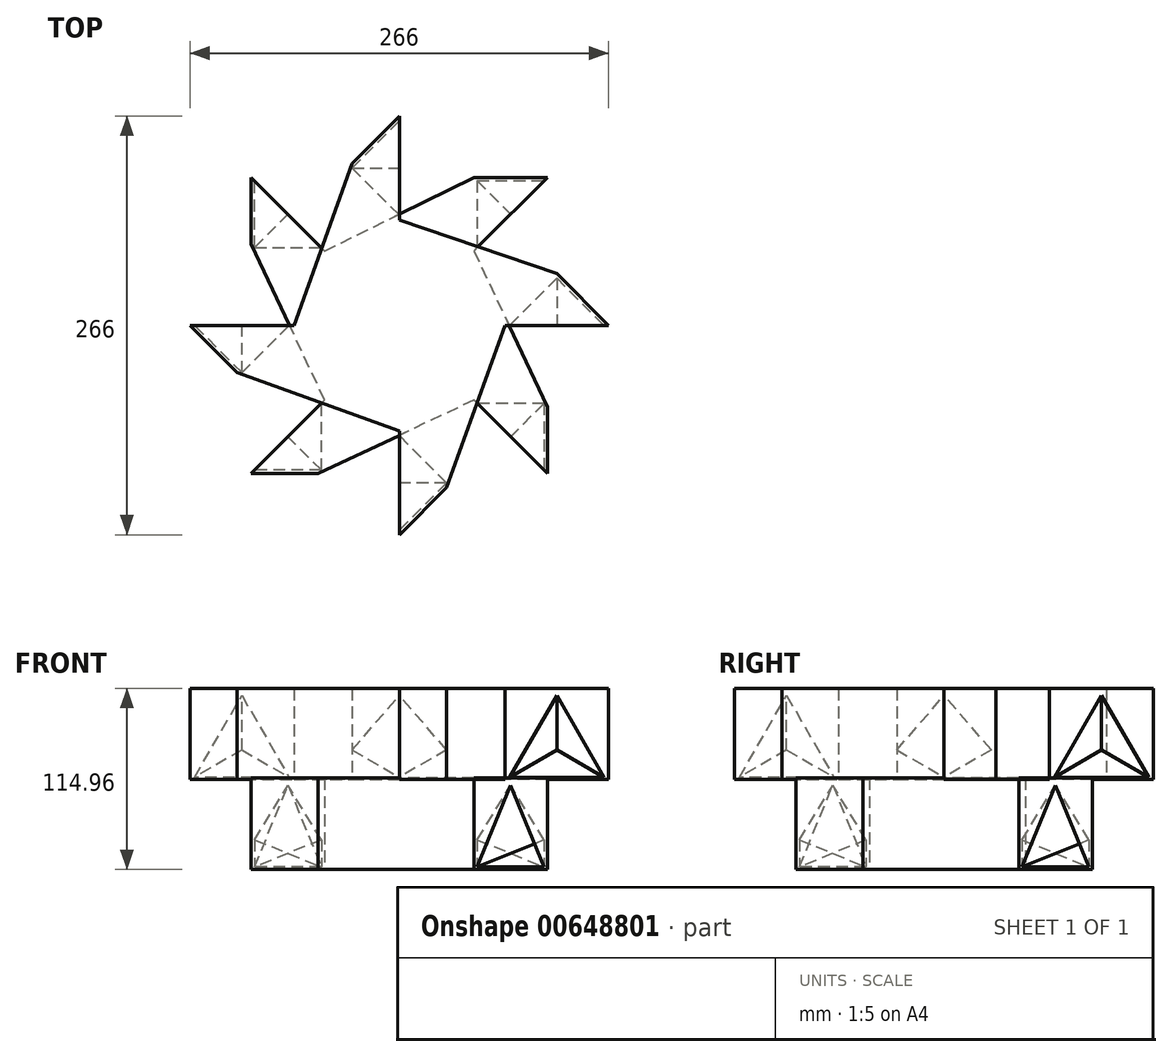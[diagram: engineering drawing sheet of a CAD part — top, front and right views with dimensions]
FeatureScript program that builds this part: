
annotation { "Feature Type Name" : "Feature", "Feature Type Description" : "" }
export const myFeature = defineFeature(function(context is Context, id is Id, definition is map)
    precondition{}
    {
        {
            var Q0;
            Q0=qCreatedBy(makeId("Front.planeOp"),FACE);
            var sketch = newSketch(context, id + "F0", { "sketchPlane" : qUnion([Q0])});
            skLineSegment(sketch, "E0", {"start": v(0, 0) * mm, "end": v(0, 38.88) * mm, "construction": true});
            skLineSegment(sketch, "E1", {"start": v(0, 0) * mm, "end": v(100, 0) * mm, "construction": true});
            skCircle(sketch, "E2.cCircle", {"center": v(100, 18.82) * mm, "radius": 34.64 * mm, "construction": true});
            skLineSegment(sketch, "E2.0", {"start": v(130, 1.5) * mm, "end": v(70, 1.5) * mm});
            skLineSegment(sketch, "E2.1", {"start": v(70, 1.5) * mm, "end": v(100, 53.46) * mm});
            skLineSegment(sketch, "E2.2", {"start": v(100, 53.46) * mm, "end": v(130, 1.5) * mm});
            skLineSegment(sketch, "E3", {"start": v(100, 0) * mm, "end": v(100, 18.82) * mm, "construction": true});
            skSolve(sketch);
        }
        {
            var Q0;
            Q0=makeQuery(id+"F0.imprint","IMPRINT",FACE,{"disambiguationData":[TD([[makeQuery(id+"F0.imprint","IMPRINT",EDGE,{"derivedFrom":sQuery(id+"F0.wireOp",EDGE,"E2.0")}),-1.0]])]});
            extrude(context, id + "F1", {"entities" : qUnion([Q0]), "oppositeDirection" : true, "depth" : 31 * mm, "offsetDistance" : 25 * mm, "hasDraft" : true, "draftAngle" : 30 * degree, "draftPullDirection" : true});
        }
        {
            var Q0;
            Q0=makeQuery(id+"F1.opExtrude","SWEPT_BODY",BODY,{"disambiguationData":[OSD([sQuery(id+"F0.wireOp",EDGE,"E2.0"),sQuery(id+"F0.wireOp",EDGE,"E2.1"),sQuery(id+"F0.wireOp",EDGE,"E2.2")])]});
            var Q1;
            Q1=sQuery(id+"F0.wireOp",EDGE,"E0");
            circularPattern(context, id + "F2", {"entities" : qUnion([Q0]), "axis" : qUnion([Q1]), "angle" : 360 * degree, "instanceCount" : 4, "equalSpace" : true});
        }
        {
            var Q0;
            Q0=qCreatedBy(makeId("Top.planeOp"),FACE);
            var sketch = newSketch(context, id + "F3", { "sketchPlane" : qUnion([Q0])});
            skLineSegment(sketch, "E4", {"start": v(133, 0) * mm, "end": v(67, 0) * mm});
            skLineSegment(sketch, "E5", {"start": v(67, 0) * mm, "end": v(30, -103) * mm});
            skLineSegment(sketch, "E6", {"start": v(30, -103) * mm, "end": v(0, -133) * mm});
            skLineSegment(sketch, "E7", {"start": v(0, -133) * mm, "end": v(0, -67) * mm});
            skLineSegment(sketch, "E8", {"start": v(0, -67) * mm, "end": v(-103, -30) * mm});
            skLineSegment(sketch, "E9", {"start": v(-103, -30) * mm, "end": v(-133, 0) * mm});
            skLineSegment(sketch, "E10", {"start": v(-133, 0) * mm, "end": v(-67, 0) * mm});
            skLineSegment(sketch, "E11", {"start": v(-67, 0) * mm, "end": v(-30, 103) * mm});
            skLineSegment(sketch, "E12", {"start": v(-30, 103) * mm, "end": v(0, 133) * mm});
            skLineSegment(sketch, "E13", {"start": v(0, 133) * mm, "end": v(0, 67) * mm});
            skLineSegment(sketch, "E14", {"start": v(0, 67) * mm, "end": v(100, 33) * mm});
            skLineSegment(sketch, "E15", {"start": v(100, 33) * mm, "end": v(133, 0) * mm});
            skSolve(sketch);
        }
        {
            var Q0;
            Q0=makeQuery(id+"F3.imprint","IMPRINT",FACE,{"disambiguationData":[TD([[makeQuery(id+"F3.imprint","IMPRINT",EDGE,{"derivedFrom":sQuery(id+"F3.wireOp",EDGE,"E4")}),-1.0]])]});
            extrude(context, id + "F4", {"entities" : qUnion([Q0]), "depth" : 60 * mm * sqrt(3) / 2 + 6 * mm, "offsetDistance" : 25 * mm});
        }
        {
            var Q0;
            Q0=makeQuery(id+"F1.opExtrude","SWEPT_BODY",BODY,{"disambiguationData":[OSD([sQuery(id+"F0.wireOp",EDGE,"E2.0"),sQuery(id+"F0.wireOp",EDGE,"E2.1"),sQuery(id+"F0.wireOp",EDGE,"E2.2")])]});
            var Q1;
            Q1=makeQuery(id+"F2.opPattern","COPY",BODY,{"derivedFrom":makeQuery(id+"F1.opExtrude","SWEPT_BODY",BODY,{"disambiguationData":[OSD([sQuery(id+"F0.wireOp",EDGE,"E2.0"),sQuery(id+"F0.wireOp",EDGE,"E2.1"),sQuery(id+"F0.wireOp",EDGE,"E2.2")])]}),"instanceName":"1"});
            var Q2;
            Q2=makeQuery(id+"F2.opPattern","COPY",BODY,{"derivedFrom":makeQuery(id+"F1.opExtrude","SWEPT_BODY",BODY,{"disambiguationData":[OSD([sQuery(id+"F0.wireOp",EDGE,"E2.0"),sQuery(id+"F0.wireOp",EDGE,"E2.1"),sQuery(id+"F0.wireOp",EDGE,"E2.2")])]}),"instanceName":"2"});
            var Q3;
            Q3=makeQuery(id+"F2.opPattern","COPY",BODY,{"derivedFrom":makeQuery(id+"F1.opExtrude","SWEPT_BODY",BODY,{"disambiguationData":[OSD([sQuery(id+"F0.wireOp",EDGE,"E2.0"),sQuery(id+"F0.wireOp",EDGE,"E2.1"),sQuery(id+"F0.wireOp",EDGE,"E2.2")])]}),"instanceName":"3"});
            var Q4;
            Q4=makeQuery(id+"F4.opExtrude","SWEPT_BODY",BODY,{"disambiguationData":[OSD([sQuery(id+"F3.wireOp",EDGE,"E4"),sQuery(id+"F3.wireOp",EDGE,"E5"),sQuery(id+"F3.wireOp",EDGE,"E6"),sQuery(id+"F3.wireOp",EDGE,"E7"),sQuery(id+"F3.wireOp",EDGE,"E8"),sQuery(id+"F3.wireOp",EDGE,"E9"),sQuery(id+"F3.wireOp",EDGE,"E10"),sQuery(id+"F3.wireOp",EDGE,"E11"),sQuery(id+"F3.wireOp",EDGE,"E12"),sQuery(id+"F3.wireOp",EDGE,"E13"),sQuery(id+"F3.wireOp",EDGE,"E14"),sQuery(id+"F3.wireOp",EDGE,"E15")])]});
            booleanBodies(context, id + "F5", {"operationType" : BooleanOperationType.SUBTRACTION, "tools" : qUnion([Q0, Q1, Q2, Q3]), "targets" : qUnion([Q4])});
        }
        {
            var Q0;
            Q0=makeQuery(id+"F4.opExtrude","SWEPT_BODY",BODY,{"disambiguationData":[OSD([sQuery(id+"F3.wireOp",EDGE,"E4"),sQuery(id+"F3.wireOp",EDGE,"E5"),sQuery(id+"F3.wireOp",EDGE,"E6"),sQuery(id+"F3.wireOp",EDGE,"E7"),sQuery(id+"F3.wireOp",EDGE,"E8"),sQuery(id+"F3.wireOp",EDGE,"E9"),sQuery(id+"F3.wireOp",EDGE,"E10"),sQuery(id+"F3.wireOp",EDGE,"E11"),sQuery(id+"F3.wireOp",EDGE,"E12"),sQuery(id+"F3.wireOp",EDGE,"E13"),sQuery(id+"F3.wireOp",EDGE,"E14"),sQuery(id+"F3.wireOp",EDGE,"E15")])]});
            var Q1;
            Q1=sQuery(id+"F0.wireOp",EDGE,"E0");
            var Q2;
            Q2=sQuery(id+"F0.wireOp",EDGE,"E0");
            transform(context, id + "F6", {"entities" : qUnion([Q0]), "transformType" : TransformType.TRANSLATION_DISTANCE, "transformDirection" : qUnion([Q2]), "distance" : 60 * mm - 3 * mm, "oppositeDirection" : true, "makeCopy" : true});
        }
        {
            var Q0;
            Q0=makeQuery(id+"F6.opPattern","COPY",BODY,{"derivedFrom":makeQuery(id+"F4.opExtrude","SWEPT_BODY",BODY,{"disambiguationData":[OSD([sQuery(id+"F3.wireOp",EDGE,"E4"),sQuery(id+"F3.wireOp",EDGE,"E5"),sQuery(id+"F3.wireOp",EDGE,"E6"),sQuery(id+"F3.wireOp",EDGE,"E7"),sQuery(id+"F3.wireOp",EDGE,"E8"),sQuery(id+"F3.wireOp",EDGE,"E9"),sQuery(id+"F3.wireOp",EDGE,"E10"),sQuery(id+"F3.wireOp",EDGE,"E11"),sQuery(id+"F3.wireOp",EDGE,"E12"),sQuery(id+"F3.wireOp",EDGE,"E13"),sQuery(id+"F3.wireOp",EDGE,"E14"),sQuery(id+"F3.wireOp",EDGE,"E15")])]}),"instanceName":"1"});
            var Q1;
            Q1=sQuery(id+"F0.wireOp",EDGE,"E0");
            transform(context, id + "F7", {"entities" : qUnion([Q0]), "transformType" : TransformType.ROTATION, "transformAxis" : qUnion([Q1]), "angle" : 45 * degree, "makeCopy" : false});
        }
    });
